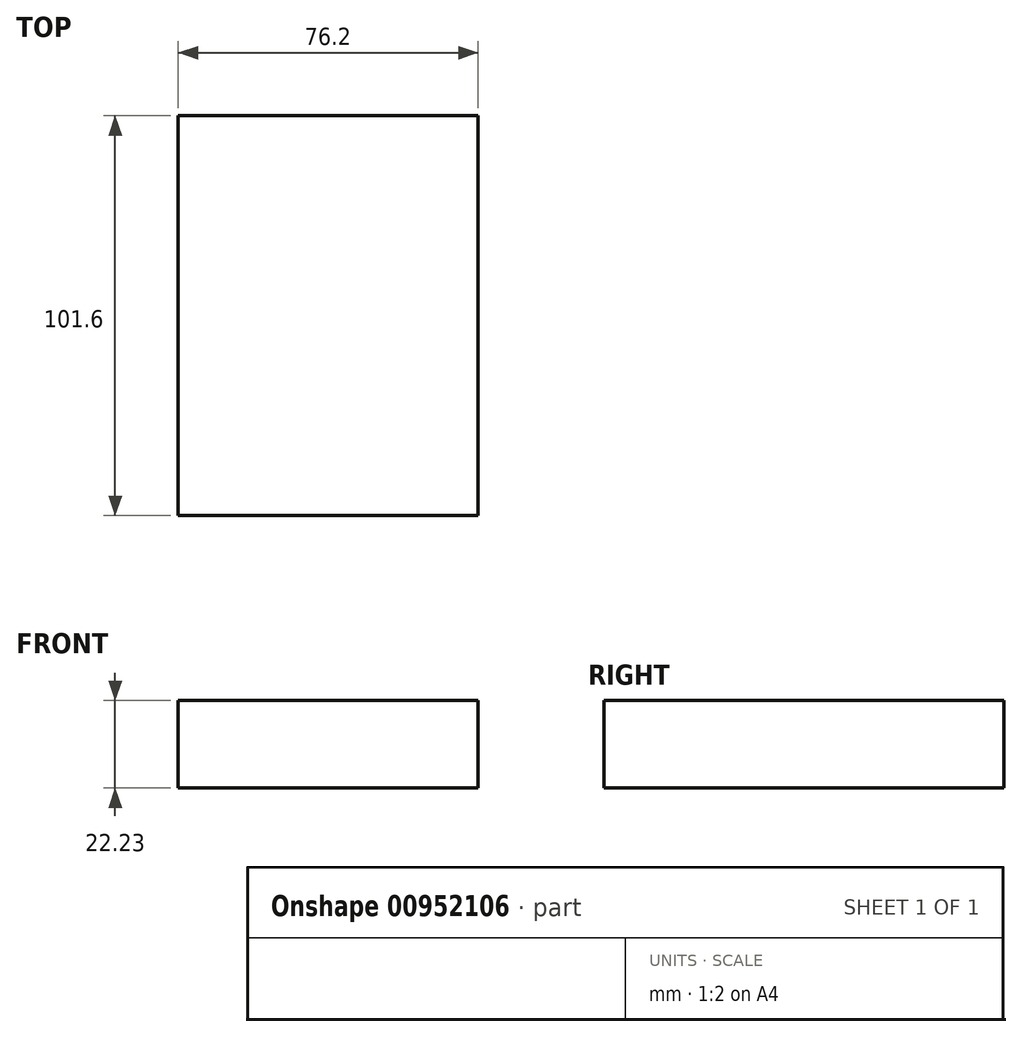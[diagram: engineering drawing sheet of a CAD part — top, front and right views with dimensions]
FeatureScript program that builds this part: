
annotation { "Feature Type Name" : "Feature", "Feature Type Description" : "" }
export const myFeature = defineFeature(function(context is Context, id is Id, definition is map)
    precondition{}
    {
        {
            var Q0;
            Q0=qCreatedBy(makeId("Top.planeOp"),FACE);
            var sketch = newSketch(context, id + "F0", { "sketchPlane" : qUnion([Q0])});
            skLineSegment(sketch, "E0.bottom", {"start": v(-38.1, 50.8) * mm, "end": v(38.1, 50.8) * mm});
            skLineSegment(sketch, "E0.top", {"start": v(-38.1, -50.8) * mm, "end": v(38.1, -50.8) * mm});
            skLineSegment(sketch, "E0.left", {"start": v(-38.1, 50.8) * mm, "end": v(-38.1, -50.8) * mm});
            skLineSegment(sketch, "E0.right", {"start": v(38.1, 50.8) * mm, "end": v(38.1, -50.8) * mm});
            skLineSegment(sketch, "E1", {"start": v(-38.1, 50.8) * mm, "end": v(38.1, -50.8) * mm});
            skSolve(sketch);
        }
        {
            var Q0;
            Q0 = qSketchRegion(id + "F0", true);
            extrude(context, id + "F1", {"entities" : qUnion([Q0]), "depth" : 22.22 * mm, "offsetDistance" : 25.4 * mm});
        }
    });
